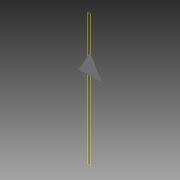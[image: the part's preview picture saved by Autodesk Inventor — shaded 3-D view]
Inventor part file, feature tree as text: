
AUTODESK INVENTOR PART (.ipt)
format: ipt  version: 2014 SP1 (Build 180222100, 222)  size: 101,376 bytes
history: native  units: in
note: dims shown in document units (in); Inventor stores cm internally (conversion verified against a paired STEP export)
features: reference x17, plane x1, extrude x1, fillet x1, sketch x1
ambient origin geometry x8: Origin, YZ Plane, XZ Plane, XY Plane, X Axis, Y Axis, Z Axis, Center Point
bodies: Solid1 (feature_tree)
feature tree (21):
  plane  "Work Plane1"
  extrude  "Extrusion1"  Depth=0.125in TaperAngle=0.0deg
  fillet  "Fillet1"  Radius=0.125in
  sketch  "Sketch1"  dims[d0=1.0in d1=0.125in d2=0.0in d3=0.125in]
  reference  "Reference1"
  reference  "Reference2"
  reference  "Reference3"
  reference  "Reference4"
  reference  "Reference5"
  reference  "Reference6"
  reference  "Reference7"
  reference  "Reference8"
  reference  "Reference9"
  reference  "Reference10"
  reference  "Reference11"
  reference  "Reference12"
  reference  "Reference13"
  reference  "Reference14"
  reference  "Reference15"
  reference  "Reference16"
  reference  "Reference17"
